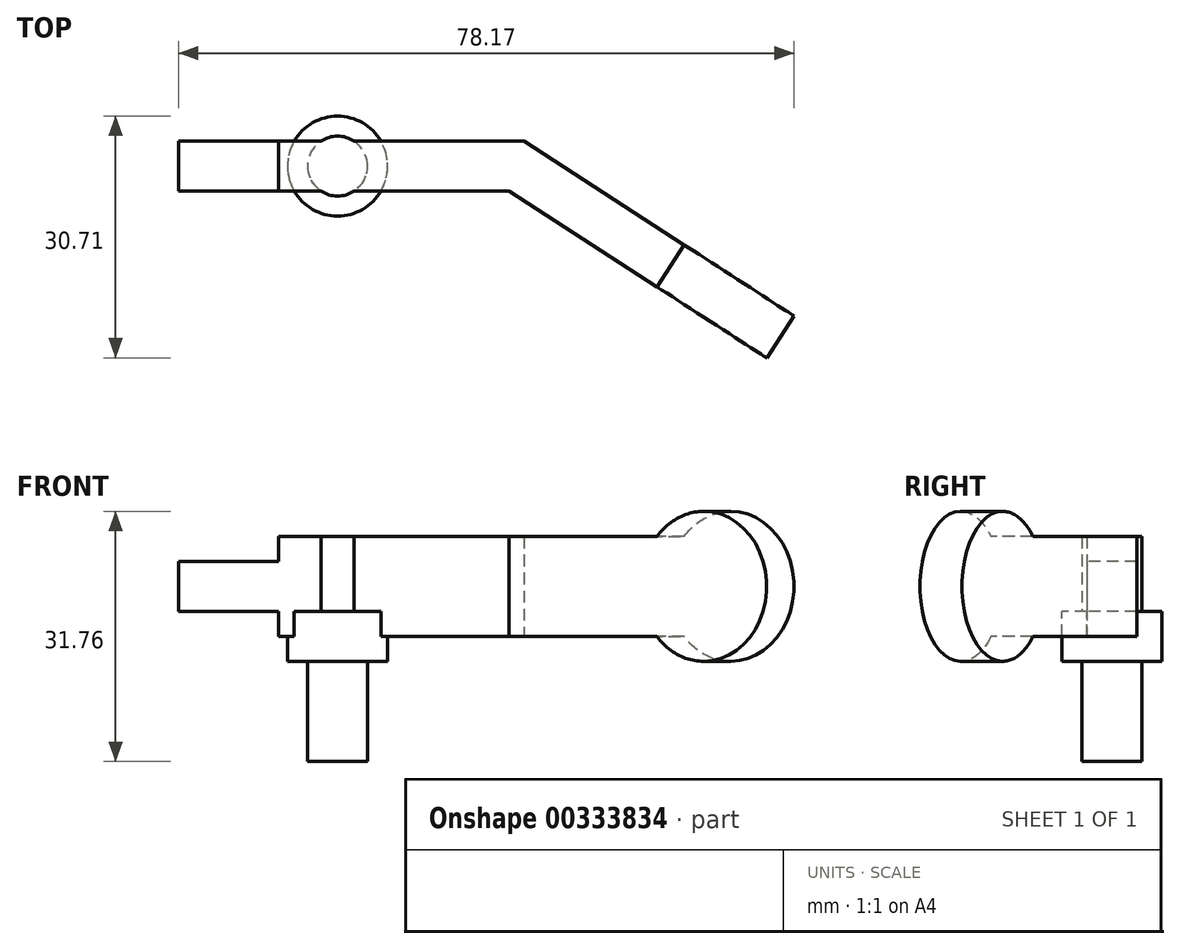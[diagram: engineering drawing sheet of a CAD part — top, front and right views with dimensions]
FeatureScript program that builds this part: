
annotation { "Feature Type Name" : "Feature", "Feature Type Description" : "" }
export const myFeature = defineFeature(function(context is Context, id is Id, definition is map)
    precondition{}
    {
        {
            var Q0;
            Q0=qCreatedBy(makeId("Top.planeOp"),FACE);
            var sketch = newSketch(context, id + "F0", { "sketchPlane" : qUnion([Q0])});
            skCircle(sketch, "E0", {"center": v(0, 0) * mm, "radius": 3.81 * mm});
            skLineSegment(sketch, "E1", {"start": v(2.1, 3.18) * mm, "end": v(23.65, 3.18) * mm});
            skLineSegment(sketch, "E2", {"start": v(-20.2, -3.18) * mm, "end": v(-2.1, -3.18) * mm});
            skLineSegment(sketch, "E3", {"start": v(21.78, -3.17) * mm, "end": v(46.52, -19.19) * mm});
            skLineSegment(sketch, "E4.0", {"start": v(23.65, 3.18) * mm, "end": v(49.97, -13.85) * mm});
            skLineSegment(sketch, "E5", {"start": v(49.97, -13.85) * mm, "end": v(46.52, -19.19) * mm});
            skLineSegment(sketch, "E6", {"start": v(-2.1, 3.18) * mm, "end": v(-20.2, 3.18) * mm});
            skLineSegment(sketch, "E7", {"start": v(-20.2, 3.18) * mm, "end": v(-20.2, -3.18) * mm});
            skPoint(sketch, "E8.orphan", {"position": v(2.1, -3.18) * mm});
            skLineSegment(sketch, "E9.trimOffspring", {"start": v(2.1, -3.18) * mm, "end": v(21.78, -3.18) * mm});
            skSolve(sketch);
        }
        {
            var Q0;
            Q0 = qSketchRegion(id + "F0", true);
            extrude(context, id + "F1", {"entities" : qUnion([Q0]), "depth" : 12.7 * mm});
        }
        {
            var Q0;
            Q0=makeQuery(id+"F1.opExtrude","CAP_FACE",FACE,{"disambiguationData":[OSD([sQuery(id+"F0.wireOp",EDGE,"E0"),sQuery(id+"F0.wireOp",EDGE,"E1"),sQuery(id+"F0.wireOp",EDGE,"E2"),sQuery(id+"F0.wireOp",EDGE,"E3"),sQuery(id+"F0.wireOp",EDGE,"E4.0"),sQuery(id+"F0.wireOp",EDGE,"E5"),sQuery(id+"F0.wireOp",EDGE,"E6"),sQuery(id+"F0.wireOp",EDGE,"E7"),sQuery(id+"F0.wireOp",EDGE,"E9.trimOffspring")])],"isStart":true});
            var sketch = newSketch(context, id + "F2", { "sketchPlane" : qUnion([Q0])});
            skCircle(sketch, "E10", {"center": v(0, 0) * mm, "radius": 3.81 * mm});
            skCircle(sketch, "E11", {"center": v(0, 0) * mm, "radius": 6.35 * mm});
            skSolve(sketch);
        }
        {
            var Q0;
            {var subQ0=sQuery(id+"F2.wireOp",EDGE,"E10");var subQ1=makeQuery(id+"F2.imprint","INTERSECT",VERTEX,{"derivedFrom":[makeQuery(id+"F1.opExtrude","CAP_EDGE",EDGE,{"disambiguationData":[OSD([sQuery(id+"F0.wireOp",EDGE,"E1")])],"isStart":true}),subQ0]});var subQ2=makeQuery(id+"F2.imprint","INTERSECT",VERTEX,{"derivedFrom":[makeQuery(id+"F1.opExtrude","CAP_EDGE",EDGE,{"disambiguationData":[OSD([sQuery(id+"F0.wireOp",EDGE,"E6")])],"isStart":true}),subQ0]});Q0=makeQuery(id+"F2.imprint","IMPRINT",FACE,{"disambiguationData":[TD([[makeQuery(id+"F2.imprint","IMPRINT",EDGE,{"disambiguationData":[TD([[subQ1,-1.0],[subQ2,1.0]])],"derivedFrom":subQ0}),-1.0]])]});}
            extrude(context, id + "F3", {"entities" : qUnion([Q0]), "operationType" : NewBodyOperationType.ADD, "depth" : 15.88 * mm});
        }
        {
            var Q0;
            {var subQ0=sQuery(id+"F2.wireOp",EDGE,"E10");var subQ1=makeQuery(id+"F1.opExtrude","CAP_EDGE",EDGE,{"disambiguationData":[OSD([sQuery(id+"F0.wireOp",EDGE,"E1")])],"isStart":true});var subQ2=makeQuery(id+"F2.imprint","INTERSECT",VERTEX,{"derivedFrom":[subQ1,subQ0]});var subQ3=makeQuery(id+"F1.opExtrude","CAP_EDGE",EDGE,{"disambiguationData":[OSD([sQuery(id+"F0.wireOp",EDGE,"E9.trimOffspring")])],"isStart":true});var subQ4=makeQuery(id+"F2.imprint","INTERSECT",VERTEX,{"derivedFrom":[subQ3,subQ0]});Q0=makeQuery(id+"F2.imprint","IMPRINT",FACE,{"disambiguationData":[TD([[makeQuery(id+"F2.imprint","IMPRINT",EDGE,{"disambiguationData":[TD([[subQ2,-1.0],[subQ4,1.0]])],"derivedFrom":subQ0}),-1.0]])]});}
            var Q1;
            {var subQ0=sQuery(id+"F2.wireOp",EDGE,"E10");var subQ1=makeQuery(id+"F1.opExtrude","CAP_EDGE",EDGE,{"disambiguationData":[OSD([sQuery(id+"F0.wireOp",EDGE,"E2")])],"isStart":true});var subQ2=makeQuery(id+"F2.imprint","INTERSECT",VERTEX,{"derivedFrom":[subQ1,subQ0]});var subQ3=makeQuery(id+"F1.opExtrude","CAP_EDGE",EDGE,{"disambiguationData":[OSD([sQuery(id+"F0.wireOp",EDGE,"E9.trimOffspring")])],"isStart":true});var subQ4=makeQuery(id+"F2.imprint","INTERSECT",VERTEX,{"derivedFrom":[subQ3,subQ0]});Q1=makeQuery(id+"F2.imprint","IMPRINT",FACE,{"disambiguationData":[TD([[makeQuery(id+"F2.imprint","IMPRINT",EDGE,{"disambiguationData":[TD([[subQ2,-1.0],[subQ4,1.0]])],"derivedFrom":subQ0}),1.0]])]});}
            var Q2;
            {var subQ0=sQuery(id+"F2.wireOp",EDGE,"E10");var subQ1=makeQuery(id+"F1.opExtrude","CAP_EDGE",EDGE,{"disambiguationData":[OSD([sQuery(id+"F0.wireOp",EDGE,"E2")])],"isStart":true});var subQ2=makeQuery(id+"F2.imprint","INTERSECT",VERTEX,{"derivedFrom":[subQ1,subQ0]});var subQ3=makeQuery(id+"F1.opExtrude","CAP_EDGE",EDGE,{"disambiguationData":[OSD([sQuery(id+"F0.wireOp",EDGE,"E6")])],"isStart":true});var subQ4=makeQuery(id+"F2.imprint","INTERSECT",VERTEX,{"derivedFrom":[subQ3,subQ0]});Q2=makeQuery(id+"F2.imprint","IMPRINT",FACE,{"disambiguationData":[TD([[makeQuery(id+"F2.imprint","IMPRINT",EDGE,{"disambiguationData":[TD([[subQ2,-1.0],[subQ4,1.0]])],"derivedFrom":subQ0}),-1.0]])]});}
            var Q3;
            {var subQ0=sQuery(id+"F2.wireOp",EDGE,"E10");var subQ1=makeQuery(id+"F1.opExtrude","CAP_EDGE",EDGE,{"disambiguationData":[OSD([sQuery(id+"F0.wireOp",EDGE,"E1")])],"isStart":true});var subQ2=makeQuery(id+"F2.imprint","INTERSECT",VERTEX,{"derivedFrom":[subQ1,subQ0]});var subQ3=makeQuery(id+"F1.opExtrude","CAP_EDGE",EDGE,{"disambiguationData":[OSD([sQuery(id+"F0.wireOp",EDGE,"E6")])],"isStart":true});var subQ4=makeQuery(id+"F2.imprint","INTERSECT",VERTEX,{"derivedFrom":[subQ3,subQ0]});Q3=makeQuery(id+"F2.imprint","IMPRINT",FACE,{"disambiguationData":[TD([[makeQuery(id+"F2.imprint","IMPRINT",EDGE,{"disambiguationData":[TD([[subQ2,-1.0],[subQ4,1.0]])],"derivedFrom":subQ0}),1.0]])]});}
            extrude(context, id + "F4", {"entities" : qUnion([Q0, Q1, Q2, Q3]), "operationType" : NewBodyOperationType.ADD, "endBound" : BoundingType.SYMMETRIC, "depth" : 6.35 * mm});
        }
        {
            var Q0;
            Q0=makeQuery(id+"F1.opExtrude","SWEPT_FACE",FACE,{"disambiguationData":[OSD([sQuery(id+"F0.wireOp",EDGE,"E3")])]});
            var sketch = newSketch(context, id + "F5", { "sketchPlane" : qUnion([Q0])});
            skCircle(sketch, "E12", {"center": v(49.48, 6.35) * mm, "radius": 9.53 * mm});
            skSolve(sketch);
        }
        {
            var Q0;
            {var subQ1=sQuery(id+"F0.wireOp",EDGE,"E3");var subQ6=makeQuery(id+"F1.opExtrude","SWEPT_EDGE",EDGE,{"disambiguationData":[OSD([subQ1,sQuery(id+"F0.wireOp",EDGE,"E5")])]});Q0=makeQuery(id+"F5.imprint","IMPRINT",FACE,{"disambiguationData":[TD([[makeQuery(id+"F5.imprint","IMPRINT",EDGE,{"derivedFrom":subQ6}),1.0]])]});}
            var Q1;
            Q1=makeQuery(id+"F1.opExtrude","SWEPT_FACE",FACE,{"disambiguationData":[OSD([sQuery(id+"F0.wireOp",EDGE,"E4.0")])]});
            extrude(context, id + "F6", {"entities" : qUnion([Q0]), "operationType" : NewBodyOperationType.ADD, "endBound" : BoundingType.UP_TO_SURFACE, "oppositeDirection" : true, "endBoundEntityFace" : qUnion([Q1]), "depth" : 25.4 * mm});
        }
        {
            var Q0;
            Q0=makeQuery(id+"F1.opExtrude","SWEPT_FACE",FACE,{"disambiguationData":[OSD([sQuery(id+"F0.wireOp",EDGE,"E2")])]});
            var sketch = newSketch(context, id + "F7", { "sketchPlane" : qUnion([Q0])});
            skLineSegment(sketch, "E13.bottom", {"start": v(-20.2, 12.7) * mm, "end": v(-7.5, 12.7) * mm});
            skLineSegment(sketch, "E13.top", {"start": v(-20.2, 9.52) * mm, "end": v(-7.5, 9.52) * mm});
            skLineSegment(sketch, "E13.left", {"start": v(-20.2, 12.7) * mm, "end": v(-20.2, 9.52) * mm});
            skLineSegment(sketch, "E13.right", {"start": v(-7.5, 12.7) * mm, "end": v(-7.5, 9.53) * mm});
            skLineSegment(sketch, "E14", {"start": v(-20.2, 6.35) * mm, "end": v(-4.8, 6.35) * mm, "construction": true});
            skLineSegment(sketch, "E15.MirrorCS", {"start": v(-20.2, 0) * mm, "end": v(-7.5, 0) * mm});
            skLineSegment(sketch, "E16.MirrorCS", {"start": v(-20.2, 3.18) * mm, "end": v(-7.5, 3.18) * mm});
            skLineSegment(sketch, "E17.MirrorCS", {"start": v(-7.5, 0) * mm, "end": v(-7.5, 3.18) * mm});
            skLineSegment(sketch, "E18.MirrorCS", {"start": v(-20.2, 0) * mm, "end": v(-20.2, 3.18) * mm});
            skSolve(sketch);
        }
        {
            var Q0;
            Q0=makeQuery(id+"F7.imprint","IMPRINT",FACE,{"disambiguationData":[TD([[makeQuery(id+"F7.imprint","IMPRINT",EDGE,{"derivedFrom":sQuery(id+"F7.wireOp",EDGE,"E13.bottom")}),-1.0]])]});
            var Q1;
            Q1=makeQuery(id+"F7.imprint","IMPRINT",FACE,{"disambiguationData":[TD([[makeQuery(id+"F7.imprint","IMPRINT",EDGE,{"derivedFrom":sQuery(id+"F7.wireOp",EDGE,"E15.MirrorCS")}),1.0]])]});
            extrude(context, id + "F8", {"entities" : qUnion([Q0, Q1]), "operationType" : NewBodyOperationType.REMOVE, "endBound" : BoundingType.THROUGH_ALL, "oppositeDirection" : true, "depth" : 25.4 * mm});
        }
    });
